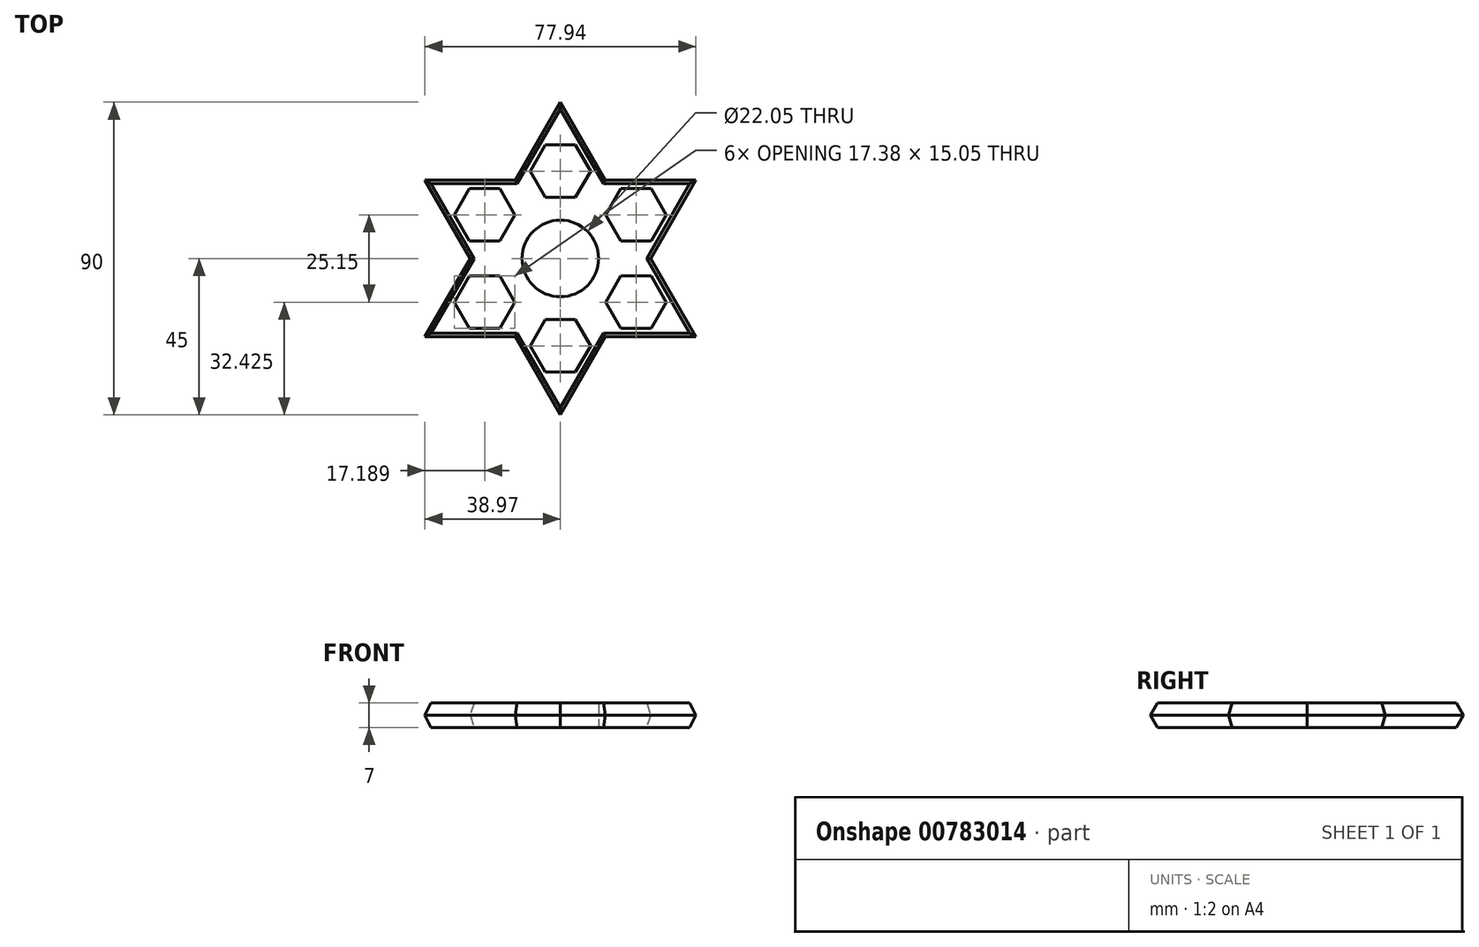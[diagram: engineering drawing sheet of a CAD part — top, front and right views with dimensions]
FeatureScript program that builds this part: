
annotation { "Feature Type Name" : "Feature", "Feature Type Description" : "" }
export const myFeature = defineFeature(function(context is Context, id is Id, definition is map)
    precondition{}
    {
        {
            var Q0;
            Q0=qCreatedBy(makeId("Top.planeOp"),FACE);
            var sketch = newSketch(context, id + "F0", { "sketchPlane" : qUnion([Q0])});
            skCircle(sketch, "E0", {"center": v(0, 0) * mm, "radius": 11.03 * mm});
            skCircle(sketch, "E1", {"center": v(0, 0) * mm, "radius": 15.03 * mm});
            skCircle(sketch, "E2.cCircle", {"center": v(0, 25.15) * mm, "radius": 7.53 * mm, "construction": true});
            skLineSegment(sketch, "E2.0", {"start": v(4.34, 17.63) * mm, "end": v(-4.34, 17.63) * mm});
            skLineSegment(sketch, "E2.1", {"start": v(-4.34, 17.63) * mm, "end": v(-8.69, 25.15) * mm});
            skLineSegment(sketch, "E2.2", {"start": v(-8.69, 25.15) * mm, "end": v(-4.34, 32.68) * mm});
            skLineSegment(sketch, "E2.3", {"start": v(-4.34, 32.68) * mm, "end": v(4.34, 32.68) * mm});
            skLineSegment(sketch, "E2.4", {"start": v(4.34, 32.68) * mm, "end": v(8.69, 25.15) * mm});
            skLineSegment(sketch, "E2.5", {"start": v(8.69, 25.15) * mm, "end": v(4.34, 17.63) * mm});
            skPoint(sketch, "E2.0.midPoint", {"position": v(0, 17.63) * mm});
            skCircle(sketch, "E3", {"center": v(0, 0) * mm, "radius": 45 * mm, "construction": true});
            skLineSegment(sketch, "E4", {"start": v(-25.98, 0) * mm, "end": v(0, 45) * mm});
            skLineSegment(sketch, "E5", {"start": v(0, 45) * mm, "end": v(25.98, 0) * mm});
            skLineSegment(sketch, "E6", {"start": v(-25.98, 0) * mm, "end": v(-15.03, 0) * mm});
            skLineSegment(sketch, "E7", {"start": v(25.98, 0) * mm, "end": v(15.03, 0) * mm});
            skSolve(sketch);
        }
        {
            var Q0;
            Q0 = qSketchRegion(id + "F0", true);
            extrude(context, id + "F1", {"entities" : qUnion([Q0]), "depth" : 7 * mm, "offsetDistance" : 25 * mm});
        }
        {
            var Q0;
            Q0=qCreatedBy(makeId("Right.planeOp"),FACE);
            var sketch = newSketch(context, id + "F2", { "sketchPlane" : qUnion([Q0])});
            skLineSegment(sketch, "E8", {"start": v(0, 0) * mm, "end": v(0, 88.25) * mm, "construction": true});
            skSolve(sketch);
        }
        {
            var Q0;
            Q0=makeQuery(id+"F1.opExtrude","CAP_EDGE",EDGE,{"disambiguationData":[OSD([sQuery(id+"F0.wireOp",EDGE,"E5")])],"isStart":false});
            var Q1;
            Q1=makeQuery(id+"F1.opExtrude","CAP_EDGE",EDGE,{"disambiguationData":[OSD([sQuery(id+"F0.wireOp",EDGE,"E4")])],"isStart":false});
            chamfer(context, id + "F3", {"entities" : qUnion([Q0, Q1]), "chamferType" : ChamferType.TWO_OFFSETS, "width1" : 3.5 * mm, "oppositeDirection" : false, "width2" : 1 * mm, "tangentPropagation" : true});
        }
        {
            var Q0;
            Q0=makeQuery(id+"F1.opExtrude","CAP_EDGE",EDGE,{"disambiguationData":[OSD([sQuery(id+"F0.wireOp",EDGE,"E4")])],"isStart":true});
            var Q1;
            Q1=makeQuery(id+"F1.opExtrude","CAP_EDGE",EDGE,{"disambiguationData":[OSD([sQuery(id+"F0.wireOp",EDGE,"E5")])],"isStart":true});
            chamfer(context, id + "F4", {"entities" : qUnion([Q0, Q1]), "chamferType" : ChamferType.TWO_OFFSETS, "width1" : 1 * mm, "oppositeDirection" : false, "width2" : 3.5 * mm, "tangentPropagation" : true});
        }
        {
            var Q0;
            Q0=makeQuery(id+"F1.opExtrude","SWEPT_BODY",BODY,{"disambiguationData":[OSD([sQuery(id+"F0.wireOp",EDGE,"E0"),sQuery(id+"F0.wireOp",EDGE,"E1"),sQuery(id+"F0.wireOp",EDGE,"E2.0"),sQuery(id+"F0.wireOp",EDGE,"E2.1"),sQuery(id+"F0.wireOp",EDGE,"E2.2"),sQuery(id+"F0.wireOp",EDGE,"E2.3"),sQuery(id+"F0.wireOp",EDGE,"E2.4"),sQuery(id+"F0.wireOp",EDGE,"E2.5"),sQuery(id+"F0.wireOp",EDGE,"E4"),sQuery(id+"F0.wireOp",EDGE,"E5"),sQuery(id+"F0.wireOp",EDGE,"E6"),sQuery(id+"F0.wireOp",EDGE,"E7")])]});
            var Q1;
            Q1=sQuery(id+"F2.wireOp",EDGE,"E8");
            circularPattern(context, id + "F5", {"operationType" : NewBodyOperationType.ADD, "entities" : qUnion([Q0]), "axis" : qUnion([Q1]), "angle" : 360 * degree, "instanceCount" : 6, "equalSpace" : true});
        }
        {
            var Q0;
            Q0=makeQuery(id+"F0.imprint","IMPRINT",FACE,{"disambiguationData":[TD([[makeQuery(id+"F0.imprint","IMPRINT",EDGE,{"derivedFrom":sQuery(id+"F0.wireOp",EDGE,"E2.0")}),-1.0]])]});
            extrude(context, id + "F6", {"entities" : qUnion([Q0]), "depth" : 7 * mm, "offsetDistance" : 25 * mm});
        }
        {
            var Q0;
            Q0=makeQuery(id+"F6.opExtrude","SWEPT_BODY",BODY,{"disambiguationData":[OSD([sQuery(id+"F0.wireOp",EDGE,"E2.0"),sQuery(id+"F0.wireOp",EDGE,"E2.1"),sQuery(id+"F0.wireOp",EDGE,"E2.2"),sQuery(id+"F0.wireOp",EDGE,"E2.3"),sQuery(id+"F0.wireOp",EDGE,"E2.4"),sQuery(id+"F0.wireOp",EDGE,"E2.5")])]});
            var Q1;
            Q1=sQuery(id+"F2.wireOp",EDGE,"E8");
            circularPattern(context, id + "F7", {"operationType" : NewBodyOperationType.REMOVE, "entities" : qUnion([Q0]), "axis" : qUnion([Q1]), "angle" : 360 * degree, "instanceCount" : 6, "equalSpace" : true});
        }
    });
